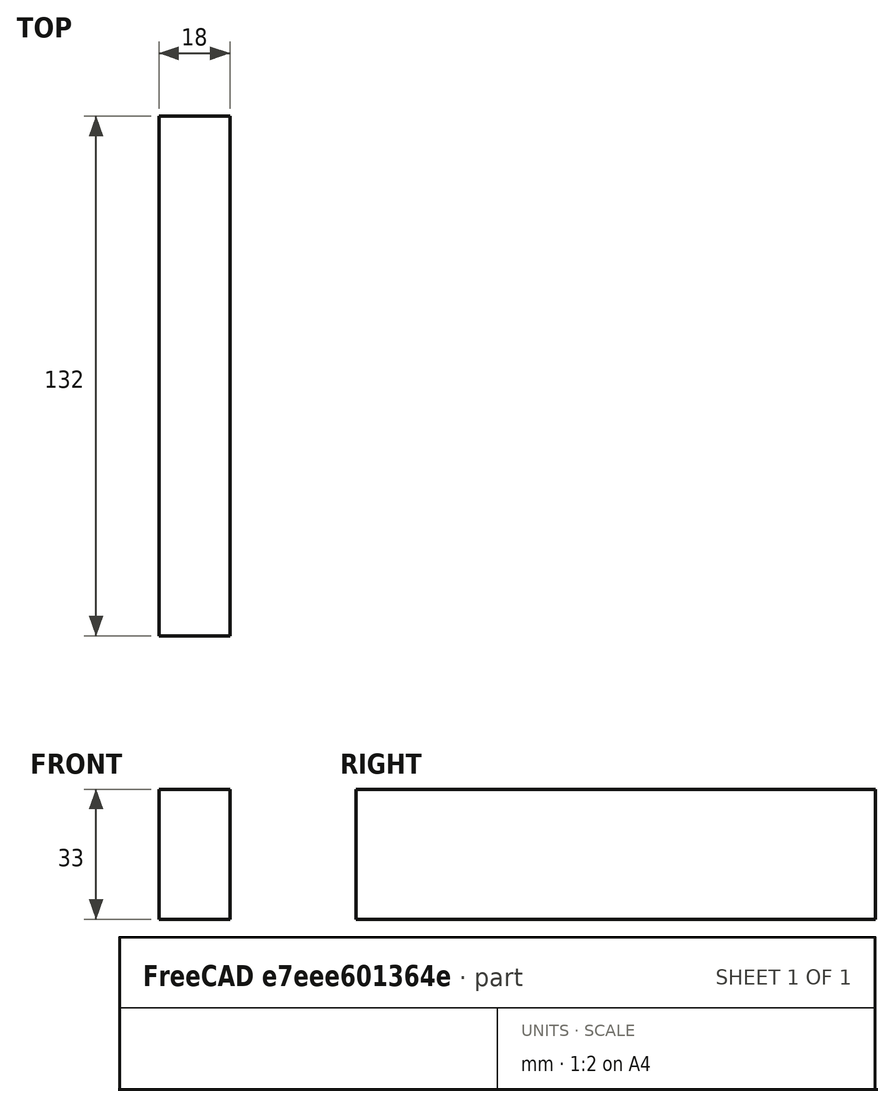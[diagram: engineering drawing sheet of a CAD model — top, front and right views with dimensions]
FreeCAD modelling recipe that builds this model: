
FCSTD DOCUMENT  (FreeCAD 0.18R4 (GitTag))
Label: drawer_side
License: All rights reserved
LicenseURL: http://en.wikipedia.org/wiki/All_rights_reserved
objects: Sketcher::SketchObject×1, PartDesign::Pad×1, PartDesign::Body×1
note: 4 computed .brp shape members not serialized (recipe doc carries the construction recipe); baked Part::Feature solids carry a one-line shape summary decoded from their .brp

FEATURE [Sketcher::SketchObject] Sketch
  MapMode = 5
  Placement = pos=(0,0,0) rot=(0.57735,0.57735,0.57735;2.0944rad)
  Support = -> [YZ_Plane]
  sketch-geometry (4):
    g0: LineSegment StartX=0 StartY=0 StartZ=0 EndX=-132 EndY=0 EndZ=0
    g1: LineSegment StartX=-132 StartY=0 StartZ=0 EndX=-132 EndY=33 EndZ=0
    g2: LineSegment StartX=-132 StartY=33 StartZ=0 EndX=0 EndY=33 EndZ=0
    g3: LineSegment StartX=0 StartY=33 StartZ=0 EndX=0 EndY=0 EndZ=0
  constraints (11):
    c: Coincident(g0,g1)
    c: Coincident(g1,g2)
    c: Coincident(g2,g3)
    c: Coincident(g3,g0)
    c: Horizontal(g0)
    c: Horizontal(g2)
    c: Vertical(g1)
    c: Vertical(g3)
    c: Coincident(g0,g-1)
    c: DistanceY(g3,g3) = 33
    c: DistanceX(g0,g0) = 132
FEATURE [PartDesign::Pad] Pad
  Length = 18
  Length2 = 100
  Placement = pos=(0,0,0) rot=(0.57735,0.57735,0.57735;2.0944rad)
  Profile = -> Sketch
  Type = 0
FEATURE [PartDesign::Body] Body
  Group = -> [Sketch,Pad]
  Origin = -> Origin
  Tip = -> Pad
